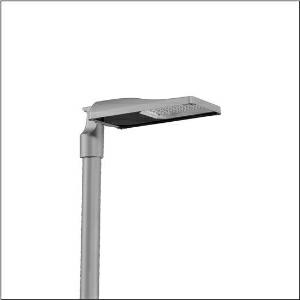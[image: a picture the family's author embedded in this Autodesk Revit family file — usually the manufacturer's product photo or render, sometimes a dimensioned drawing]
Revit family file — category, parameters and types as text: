
# Revit family: streetlight_sl_31_mini___st1_0a_5xh2d71b08ga_5698
name_source: partatom
category: Lighting Fixtures
units: mm (PartAtom-declared; Revit-internal decimal feet)

## family parameters
Cut with Voids When Loaded = No
Host = Face
Light Source = No
Part Type = Normal
Room Calculation Point = No
Round Connector Dimension = Use Diameter
Shared = No

## types (1)
- --- (1 x LED, 4620 lm, 37.3 W, 2200K)
    Apparent Load = 37 VA
    CIE Flux Codes = 37 72 97 100 100
    Color Rendering = 70
    Color Temperature = 2200K
    Default Elevation = 1800 mm
    Description = Streetlight SL 31 mini Easy, LST, Desk-Remote mast luminaire for post-top, side-entry; light control with lens of PMMA; light distribution: ST1.0a, direct asymmetric distribution, for standard-compliant lighting for roads and squares; LED: luminous flux: 4.620lm, light colour: 722, colour temperature: 2200K; luminous efficacy: 123,9lm/W; control: pre-setting: linear dimming characteristic, flexible luminous flux parameterisation, time-dependent luminous flux control, constant luminous flux control, power reduction, intelligent temperature release in ECG and LED module, overheat protection; luminaire housing, of diecast aluminium, SITECO metallic grey (DB 702S), corrosivity category C5 high according to DIN EN ISO 12944; cover of toughened safety glass, transparent, mast flange of diecast aluminium, SITECO metallic grey (DB 702S), spigot size: 76/60mm, mast flange included unmounted; cable length: 6,5m, connection cable pre-assembled; mains connection: 220..240V, AC, 50/60Hz; power consumption (at start of service life): 37,3W / (at end of service life): 38,7W / (with reduced operation 50%): 17,3W; protection rating (complete): IP66; insulation class (complete): insulation class II (safety insulation); impact resistance: IK10; certification: CE, ENEC, ENEC+, VDE, UKCA; permissible operating ambient temperature for outdoor applications: -40..+50°C; packaging unit: 1 piece

Light Distribution: ST1.0a
    Height = 76 mm
    Lamp = 1 x LED
    Lamp Light Flux = 4620 lm
    Lamp Power = 37.3 W
    Lamp count = 1
    Length = 547 mm
    Luminous efficacy = 124 lm/W
    Manufacturer = Siteco
    ModVariant = No
    Model = 5XH2D71B08GA
    Number of Poles = 1
    OnlyDefault = Yes
    Power Factor = 1
    Product Name = Streetlight SL 31 mini | ST1.0a
    Product group = mast luminaire | pylon top
    ProductGroupID = 6100
    Protection Class = Protection class II
    Protection Degree = IP 66
    RLX_Detail_Level = 1
    RLX_Emergency_Light_Flux = 0 lm
    RLX_Emergency_Type = 0
    RLX_Emergency_Type_DB = No
    RlxData = <blob elided: 39697 chars, md5=0c6dda35>
    Socket = socket
    Standby Power = 0 W
    System Light Flux = 4620 lm
    System Power = 37 W
    Type Comments = factory setting: luminous flux: 100 % | dim-lin: 254 | 386 mA
    Type Image = l_1300326.jpg
    URL = http://relux.com
    VarID = @adj_009475
    Voltage = 0 V
    Weight = 0.00 kg
    Width = 265 mm

## geometry (parser evidence)
native form markers: Blend x4, Sweep x9
no freeform markers — native parametric forms only
